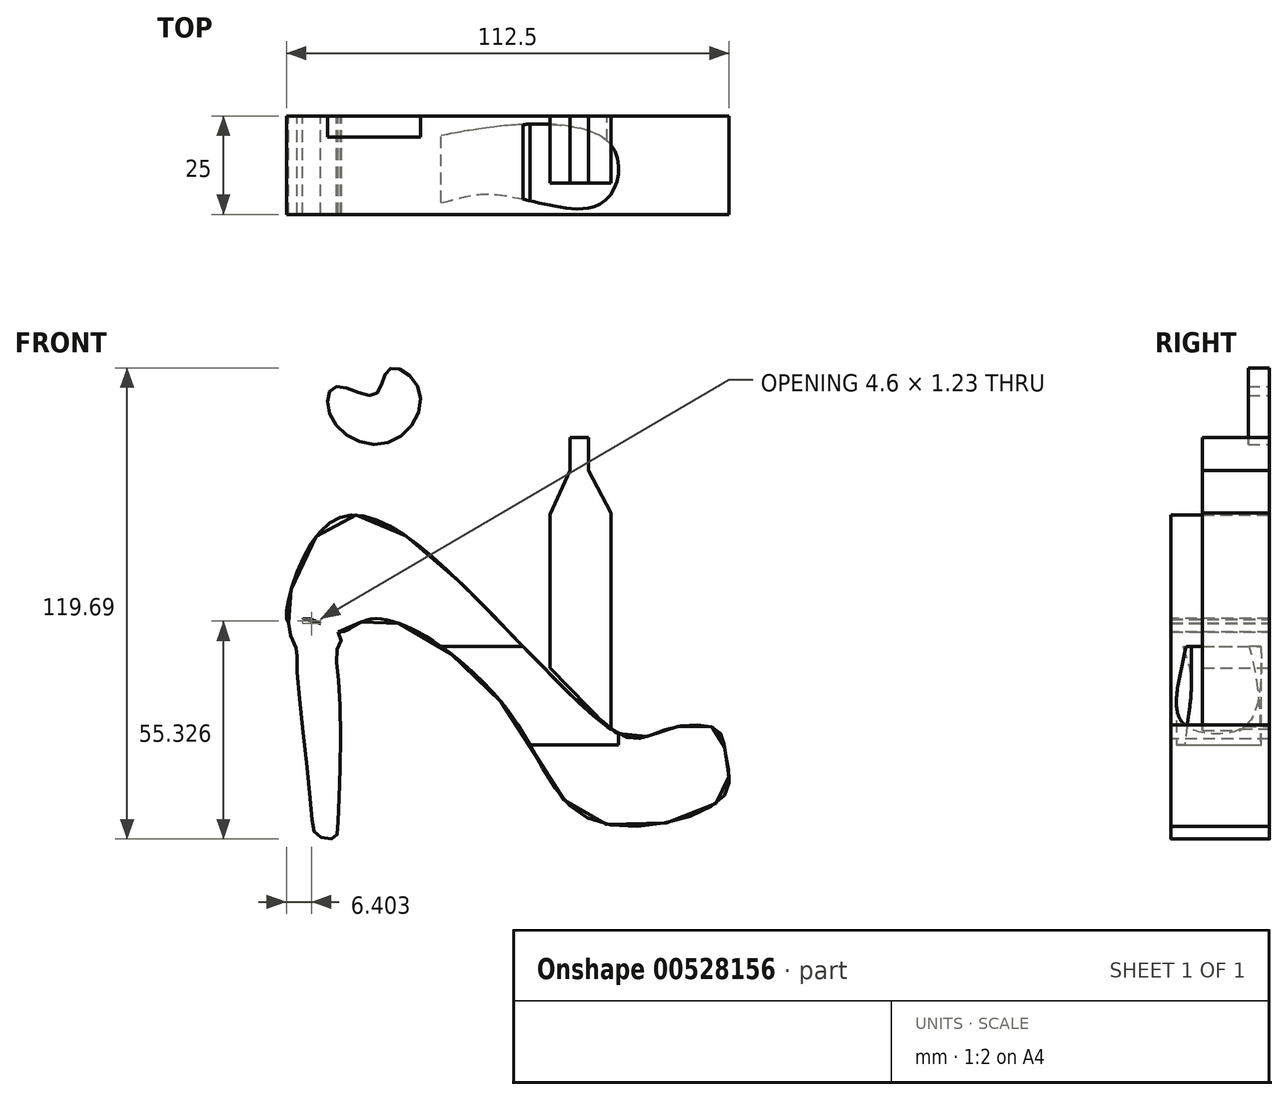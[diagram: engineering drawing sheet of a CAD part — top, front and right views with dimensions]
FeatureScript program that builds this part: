
annotation { "Feature Type Name" : "Feature", "Feature Type Description" : "" }
export const myFeature = defineFeature(function(context is Context, id is Id, definition is map)
    precondition{}
    {
        {
            var Q0;
            Q0=qCreatedBy(makeId("Front.planeOp"),FACE);
            var sketch = newSketch(context, id + "F0", { "sketchPlane" : qUnion([Q0])});
            skFitSpline(sketch, "E0", {"points": [v(-59.2, 6.52) * mm, v(-46.46, 3.12) * mm, v(-47.02, 0) * mm, v(-46.74, -11.05) * mm, v(-47.02, -45.04) * mm, v(-48.16, -48.72) * mm, v(-52.4, -47.87) * mm, v(-53.82, -41.92) * mm, v(-57.5, -4.25) * mm, v(-57.79, 0) * mm, v(-59.2, 6.52) * mm]});
            skSolve(sketch);
        }
        {
            var Q0;
            Q0=qCreatedBy(makeId("Front.planeOp"),FACE);
            var sketch = newSketch(context, id + "F1", { "sketchPlane" : qUnion([Q0])});
            skFitSpline(sketch, "E1", {"points": [v(-46.74, 3.68) * mm, v(-38.24, 7.08) * mm, v(-3.97, -16.15) * mm, v(17.85, -44.2) * mm, v(50.7, -38.24) * mm, v(51.56, -28.33) * mm, v(49, -20.96) * mm, v(35.7, -21.25) * mm, v(26.06, -22.95) * mm, v(-16.71, 17) * mm, v(-49.57, 31.16) * mm, v(-59.77, 6.23) * mm, v(-54.96, 7.08) * mm, v(-46.74, 3.68) * mm]});
            skSolve(sketch);
        }
        {
            var Q0;
            Q0=makeQuery(id+"F1.imprint","IMPRINT",FACE,{"disambiguationData":[TD([[makeQuery(id+"F1.imprint","IMPRINT",EDGE,{"derivedFrom":sQuery(id+"F1.wireOp",EDGE,"E1")}),1.0]])]});
            var sketch = newSketch(context, id + "F2", { "sketchPlane" : qUnion([Q0])});
            skFitSpline(sketch, "E2", {"points": [v(11.61, -32.3) * mm, v(15.86, -34.84) * mm, v(21.53, -34) * mm, v(51.56, -28.33) * mm, v(49.86, -39.66) * mm, v(18.13, -44.76) * mm, v(5.67, -32.3) * mm, v(-3.4, -16.43) * mm, v(11.61, -32.3) * mm]});
            skSolve(sketch);
        }
        {
            var Q0;
            {var subQ0=sQuery(id+"F2.wireOp",EDGE,"E2");var subQ1=makeQuery(id+"F1.imprint","IMPRINT",EDGE,{"derivedFrom":sQuery(id+"F1.wireOp",EDGE,"E1")});var subQ2=makeQuery(id+"F2.imprint","INTERSECT",VERTEX,{"disambiguationData":[OD(0.0)],"derivedFrom":[subQ1,subQ0]});Q0=makeQuery(id+"F2.imprint","IMPRINT",FACE,{"disambiguationData":[TD([[makeQuery(id+"F2.imprint","IMPRINT",EDGE,{"disambiguationData":[TD([[subQ2,-1.0]])],"derivedFrom":subQ0}),1.0]])]});}
            extrude(context, id + "F3", {"entities" : qUnion([Q0]), "depth" : 10.2 * mm, "offsetDistance" : 25 * mm});
        }
        {
            var Q0;
            Q0=makeQuery(id+"F1.imprint","IMPRINT",FACE,{"disambiguationData":[TD([[makeQuery(id+"F1.imprint","IMPRINT",EDGE,{"derivedFrom":sQuery(id+"F1.wireOp",EDGE,"E1")}),1.0]])]});
            var Q1;
            Q1=makeQuery(id+"F0.imprint","IMPRINT",FACE,{"disambiguationData":[TD([[makeQuery(id+"F0.imprint","IMPRINT",EDGE,{"derivedFrom":sQuery(id+"F0.wireOp",EDGE,"E0")}),-1.0]])]});
            extrude(context, id + "F4", {"entities" : qUnion([Q0, Q1]), "operationType" : NewBodyOperationType.ADD, "depth" : 25 * mm, "offsetDistance" : 25 * mm});
        }
        {
            var Q0;
            Q0=qCreatedBy(makeId("Front.planeOp"),FACE);
            var sketch = newSketch(context, id + "F5", { "sketchPlane" : qUnion([Q0])});
            skFitSpline(sketch, "E3", {"points": [v(-34.28, 51.84) * mm, v(-48.72, 58.07) * mm, v(-47.59, 66) * mm, v(-37.68, 64.02) * mm, v(-34, 70.54) * mm, v(-26.34, 64.87) * mm, v(-34.28, 51.84) * mm]});
            skSolve(sketch);
        }
        {
            var Q0;
            Q0=makeQuery(id+"F5.imprint","IMPRINT",FACE,{"disambiguationData":[TD([[makeQuery(id+"F5.imprint","IMPRINT",EDGE,{"derivedFrom":sQuery(id+"F5.wireOp",EDGE,"E3")}),-1.0]])]});
            extrude(context, id + "F6", {"entities" : qUnion([Q0]), "depth" : 5.4 * mm, "offsetDistance" : 25 * mm});
        }
        {
            var Q0;
            Q0=qCreatedBy(makeId("Front.planeOp"),FACE);
            var sketch = newSketch(context, id + "F7", { "sketchPlane" : qUnion([Q0])});
            skFitSpline(sketch, "E4", {"points": [v(-24.08, 23.8) * mm, v(-20.4, 34.28) * mm, v(-32, 42.5) * mm, v(-34.84, 49.86) * mm, v(-34.84, 51.27) * mm, v(-32.58, 48.16) * mm, v(-30.31, 43.9) * mm, v(-19.83, 36.54) * mm, v(-19.26, 28.04) * mm, v(-24.08, 23.8) * mm]});
            skSolve(sketch);
        }
        {
            var Q0;
            Q0=sQuery(id+"F7.wireOp",EDGE,"E4");
            extrude(context, id + "F8", {"bodyType" : ToolBodyType.SURFACE, "surfaceEntities" : qUnion([Q0]), "depth" : 3.8 * mm, "offsetDistance" : 25 * mm});
        }
        {
            var Q0;
            Q0=qCreatedBy(makeId("Top.planeOp"),FACE);
            var sketch = newSketch(context, id + "F9", { "sketchPlane" : qUnion([Q0])});
            skFitSpline(sketch, "E5", {"points": [v(-24.64, -5.95) * mm, v(-33.43, -11.9) * mm, v(-25.5, -21.81) * mm, v(-9.06, -19.83) * mm, v(19.55, -22.38) * mm, v(21.53, -6.52) * mm, v(-24.64, -5.95) * mm]});
            skSolve(sketch);
        }
        {
            var Q0;
            Q0=makeQuery(id+"F9.imprint","IMPRINT",FACE,{"disambiguationData":[TD([[makeQuery(id+"F9.imprint","IMPRINT",EDGE,{"derivedFrom":sQuery(id+"F9.wireOp",EDGE,"E5")}),1.0]])]});
            extrude(context, id + "F10", {"entities" : qUnion([Q0]), "operationType" : NewBodyOperationType.REMOVE, "oppositeDirection" : true, "depth" : 25 * mm, "offsetDistance" : 25 * mm});
        }
        {
            var Q0;
            Q0=qCreatedBy(makeId("Front.planeOp"),FACE);
            var sketch = newSketch(context, id + "F11", { "sketchPlane" : qUnion([Q0])});
            skLineSegment(sketch, "E6", {"start": v(6.79, 33.63) * mm, "end": v(6.79, -5.45) * mm});
            skLineSegment(sketch, "E7", {"start": v(6.79, -5.45) * mm, "end": v(22.28, -21.28) * mm});
            skLineSegment(sketch, "E8", {"start": v(22.28, -21.28) * mm, "end": v(22.28, 33.97) * mm});
            skLineSegment(sketch, "E9", {"start": v(22.28, 33.97) * mm, "end": v(16.56, 44.75) * mm});
            skLineSegment(sketch, "E10", {"start": v(16.56, 44.75) * mm, "end": v(16.56, 53.17) * mm});
            skLineSegment(sketch, "E11", {"start": v(16.56, 53.17) * mm, "end": v(11.84, 53.17) * mm});
            skLineSegment(sketch, "E12", {"start": v(11.84, 53.17) * mm, "end": v(11.84, 44.75) * mm});
            skLineSegment(sketch, "E13", {"start": v(11.84, 44.75) * mm, "end": v(6.79, 33.63) * mm});
            skSolve(sketch);
        }
        {
            var Q0;
            Q0=makeQuery(id+"F11.imprint","IMPRINT",FACE,{"disambiguationData":[TD([[makeQuery(id+"F11.imprint","IMPRINT",EDGE,{"derivedFrom":sQuery(id+"F11.wireOp",EDGE,"E6")}),1.0]])]});
            extrude(context, id + "F12", {"entities" : qUnion([Q0]), "operationType" : NewBodyOperationType.ADD, "depth" : 17 * mm, "offsetDistance" : 25 * mm});
        }
    });
